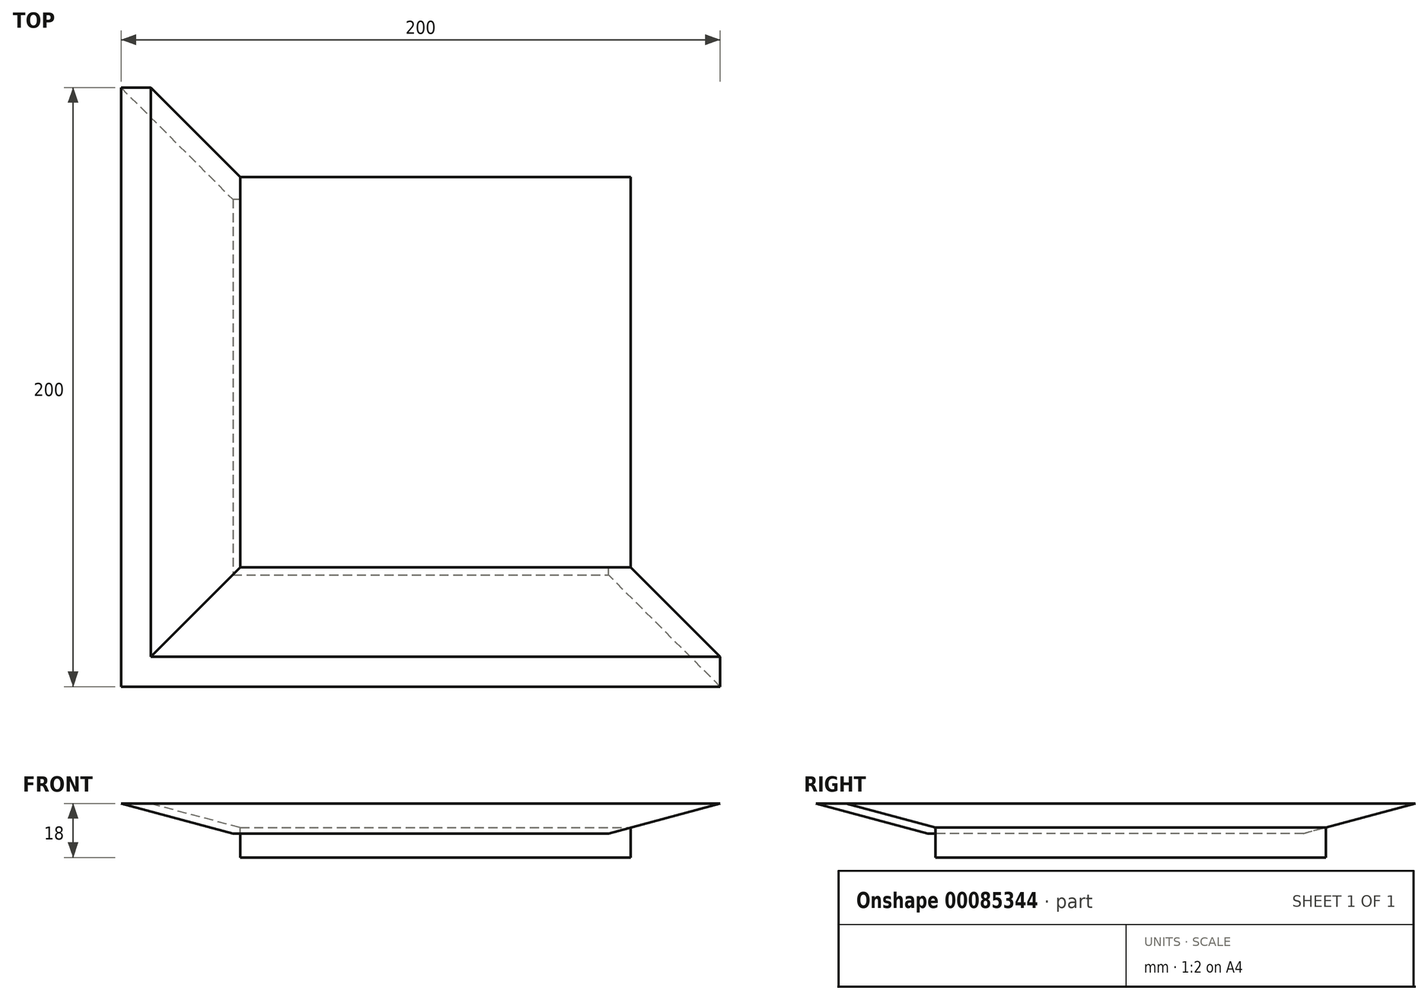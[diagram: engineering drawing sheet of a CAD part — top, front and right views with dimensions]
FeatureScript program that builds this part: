
annotation { "Feature Type Name" : "Feature", "Feature Type Description" : "" }
export const myFeature = defineFeature(function(context is Context, id is Id, definition is map)
    precondition{}
    {
        {
            var Q0;
            Q0=qCreatedBy(makeId("Top.planeOp"),FACE);
            var sketch = newSketch(context, id + "F0", { "sketchPlane" : qUnion([Q0])});
            skLineSegment(sketch, "E0.bottom", {"start": v(-104.33, 99.75) * mm, "end": v(95.67, 99.75) * mm});
            skLineSegment(sketch, "E0.top", {"start": v(-104.33, -100.25) * mm, "end": v(95.67, -100.25) * mm});
            skLineSegment(sketch, "E0.left", {"start": v(-104.33, 99.75) * mm, "end": v(-104.33, -100.25) * mm});
            skLineSegment(sketch, "E0.right", {"start": v(95.67, 99.75) * mm, "end": v(95.67, -100.25) * mm});
            skSolve(sketch);
        }
        {
            var Q0;
            Q0=makeQuery(id+"F0.imprint","IMPRINT",FACE,{"disambiguationData":[TD([[makeQuery(id+"F0.imprint","IMPRINT",EDGE,{"derivedFrom":sQuery(id+"F0.wireOp",EDGE,"E0.bottom")}),-1.0]])]});
            extrude(context, id + "F1", {"entities" : qUnion([Q0]), "oppositeDirection" : true, "depth" : 10 * mm, "hasDraft" : true, "draftAngle" : 75 * degree, "draftPullDirection" : true});
        }
        {
            var Q0;
            Q0=qCreatedBy(makeId("Top.planeOp"),FACE);
            var sketch = newSketch(context, id + "F2", { "sketchPlane" : qUnion([Q0])});
            skLineSegment(sketch, "E1.bottom", {"start": v(-94.33, 99.75) * mm, "end": v(95.67, 99.75) * mm});
            skLineSegment(sketch, "E1.top", {"start": v(-94.33, -90.25) * mm, "end": v(95.67, -90.25) * mm});
            skLineSegment(sketch, "E1.left", {"start": v(-94.33, 99.75) * mm, "end": v(-94.33, -90.25) * mm});
            skLineSegment(sketch, "E1.right", {"start": v(95.67, 99.75) * mm, "end": v(95.67, -90.25) * mm});
            skLineSegment(sketch, "E2.0", {"start": v(-104.33, 99.75) * mm, "end": v(-104.33, -100.25) * mm});
            skLineSegment(sketch, "E3.0", {"start": v(-104.33, 99.75) * mm, "end": v(95.67, 99.75) * mm});
            skSolve(sketch);
        }
        {
            var Q0;
            Q0=makeQuery(id+"F2.imprint","IMPRINT",FACE,{"disambiguationData":[TD([[makeQuery(id+"F2.imprint","IMPRINT",EDGE,{"derivedFrom":sQuery(id+"F2.wireOp",EDGE,"E1.bottom")}),-1.0]])]});
            extrude(context, id + "F3", {"entities" : qUnion([Q0]), "operationType" : NewBodyOperationType.REMOVE, "oppositeDirection" : true, "depth" : 8 * mm, "hasDraft" : true, "draftAngle" : 75 * degree, "draftPullDirection" : true});
        }
        {
            var Q0;
            Q0=makeQuery(id+"F3.boolean.opBoolean","COPY",FACE,{"derivedFrom":makeQuery(id+"F3.opExtrude","CAP_FACE",FACE,{"disambiguationData":[OSD([sQuery(id+"F2.wireOp",EDGE,"E1.bottom"),sQuery(id+"F2.wireOp",EDGE,"E1.top"),sQuery(id+"F2.wireOp",EDGE,"E1.left"),sQuery(id+"F2.wireOp",EDGE,"E1.right")])],"isStart":false})});
            extrude(context, id + "F4", {"entities" : qUnion([Q0]), "operationType" : NewBodyOperationType.ADD, "oppositeDirection" : true, "depth" : 10 * mm});
        }
    });
